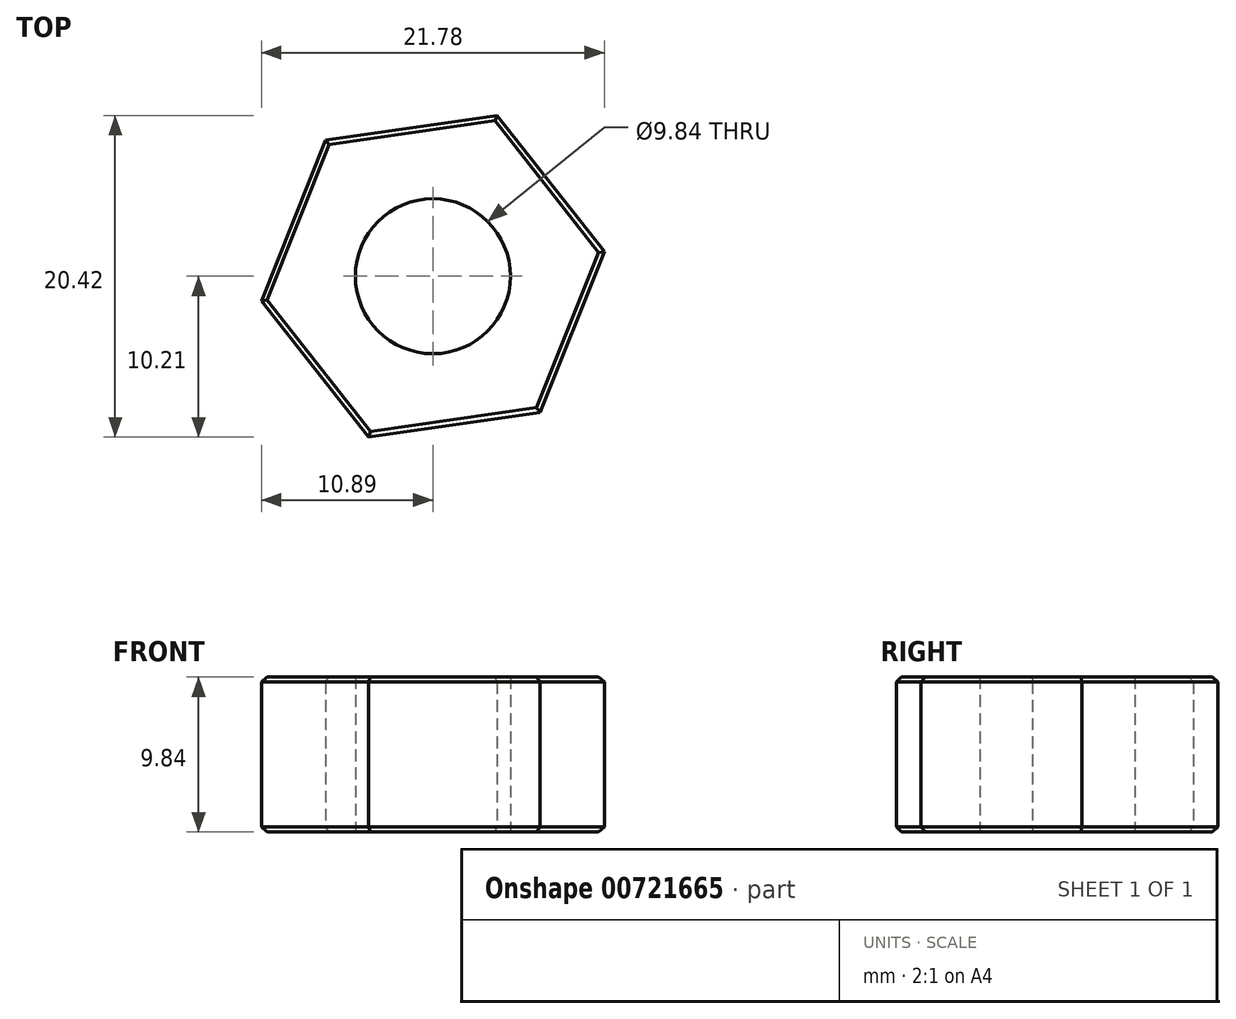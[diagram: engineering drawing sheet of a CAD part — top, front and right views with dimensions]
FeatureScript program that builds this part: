
annotation { "Feature Type Name" : "Feature", "Feature Type Description" : "" }
export const myFeature = defineFeature(function(context is Context, id is Id, definition is map)
    precondition{}
    {
        {
            var Q0;
            Q0=qCreatedBy(makeId("Top.planeOp"),FACE);
            var sketch = newSketch(context, id + "F0", { "sketchPlane" : qUnion([Q0])});
            skCircle(sketch, "E0.cCircle", {"center": v(0, 0) * mm, "radius": 9.53 * mm, "construction": true});
            skLineSegment(sketch, "E0.0", {"start": v(4.08, 10.21) * mm, "end": v(10.89, 1.57) * mm});
            skLineSegment(sketch, "E0.1", {"start": v(10.89, 1.57) * mm, "end": v(6.8, -8.64) * mm});
            skLineSegment(sketch, "E0.2", {"start": v(6.8, -8.64) * mm, "end": v(-4.08, -10.21) * mm});
            skLineSegment(sketch, "E0.3", {"start": v(-4.08, -10.21) * mm, "end": v(-10.89, -1.57) * mm});
            skLineSegment(sketch, "E0.4", {"start": v(-10.89, -1.57) * mm, "end": v(-6.8, 8.64) * mm});
            skLineSegment(sketch, "E0.5", {"start": v(-6.8, 8.64) * mm, "end": v(4.08, 10.21) * mm});
            skPoint(sketch, "E0.0.midPoint", {"position": v(7.48, 5.9) * mm});
            skCircle(sketch, "E1", {"center": v(0, 0) * mm, "radius": 4.92 * mm});
            skSolve(sketch);
        }
        {
            var Q0;
            Q0 = qSketchRegion(id + "F0", true);
            extrude(context, id + "F1", {"entities" : qUnion([Q0]), "depth" : 9.84 * mm, "offsetDistance" : 25.4 * mm});
        }
        {
            var Q0;
            Q0=makeQuery(id+"F1.opExtrude","CAP_EDGE",EDGE,{"disambiguationData":[OSD([sQuery(id+"F0.wireOp",EDGE,"E0.4")])],"isStart":false});
            var Q1;
            Q1=makeQuery(id+"F1.opExtrude","CAP_EDGE",EDGE,{"disambiguationData":[OSD([sQuery(id+"F0.wireOp",EDGE,"E0.5")])],"isStart":false});
            var Q2;
            Q2=makeQuery(id+"F1.opExtrude","CAP_EDGE",EDGE,{"disambiguationData":[OSD([sQuery(id+"F0.wireOp",EDGE,"E0.0")])],"isStart":false});
            var Q3;
            Q3=makeQuery(id+"F1.opExtrude","CAP_EDGE",EDGE,{"disambiguationData":[OSD([sQuery(id+"F0.wireOp",EDGE,"E0.1")])],"isStart":false});
            var Q4;
            Q4=makeQuery(id+"F1.opExtrude","CAP_EDGE",EDGE,{"disambiguationData":[OSD([sQuery(id+"F0.wireOp",EDGE,"E0.2")])],"isStart":false});
            var Q5;
            Q5=makeQuery(id+"F1.opExtrude","CAP_EDGE",EDGE,{"disambiguationData":[OSD([sQuery(id+"F0.wireOp",EDGE,"E0.3")])],"isStart":false});
            var Q6;
            Q6=makeQuery(id+"F1.opExtrude","CAP_EDGE",EDGE,{"disambiguationData":[OSD([sQuery(id+"F0.wireOp",EDGE,"E0.2")])],"isStart":true});
            var Q7;
            Q7=makeQuery(id+"F1.opExtrude","CAP_EDGE",EDGE,{"disambiguationData":[OSD([sQuery(id+"F0.wireOp",EDGE,"E0.1")])],"isStart":true});
            var Q8;
            Q8=makeQuery(id+"F1.opExtrude","CAP_EDGE",EDGE,{"disambiguationData":[OSD([sQuery(id+"F0.wireOp",EDGE,"E0.0")])],"isStart":true});
            var Q9;
            Q9=makeQuery(id+"F1.opExtrude","CAP_EDGE",EDGE,{"disambiguationData":[OSD([sQuery(id+"F0.wireOp",EDGE,"E0.5")])],"isStart":true});
            var Q10;
            Q10=makeQuery(id+"F1.opExtrude","CAP_EDGE",EDGE,{"disambiguationData":[OSD([sQuery(id+"F0.wireOp",EDGE,"E0.4")])],"isStart":true});
            var Q11;
            Q11=makeQuery(id+"F1.opExtrude","CAP_EDGE",EDGE,{"disambiguationData":[OSD([sQuery(id+"F0.wireOp",EDGE,"E0.3")])],"isStart":true});
            chamfer(context, id + "F2", {"entities" : qUnion([Q0, Q1, Q2, Q3, Q4, Q5, Q6, Q7, Q8, Q9, Q10, Q11]), "width" : 0.32 * mm, "tangentPropagation" : true});
        }
    });
